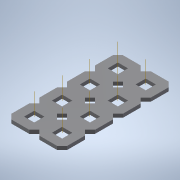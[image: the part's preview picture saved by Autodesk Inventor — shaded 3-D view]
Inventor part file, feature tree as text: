
AUTODESK INVENTOR PART (.ipt)
format: ipt  version: 2020 (Build 240168000, 168)  size: 1,142,784 bytes
history: native  units: in
note: dims shown in document units (in); Inventor stores cm internally (conversion verified against a paired STEP export)
features: other x17, extrude x2, plane x2, split x2, pattern_linear x1, imported_body x1
ambient origin geometry x8: Origin, YZ Plane, XZ Plane, XY Plane, X Axis, Y Axis, Z Axis, Center Point
bodies: Body1 (feature_tree)
feature tree (25):
  other  "Diamond-Pattern"
  other  "Plate"
  extrude  "length cut"  TaperAngle=0.0deg  [1 undecoded]
  extrude  "width cut"  TaperAngle=0.0deg  [1 undecoded]
  other  "constraint axis"
  pattern_linear  "constraint axes"  Spacing1=0.5in  [1 undecoded]
  other  "front plane"
  other  "right plane"
  plane  "Work Plane5"
  split  "Split1"
  plane  "Work Plane6"
  split  "Split2"
  imported_body  "Base1"
  other  "length profile"
  other  "width profile"
  other  "Work Point1"
  other  "Work Axis36"
  other  "Work Axis40"
  other  "Work Axis42"
  other  "back plane"
  other  "left plane"
  other  "Work Axis170"
  other  "Work Axis171"
  other  "Work Axis175"
  other  "Work Axis176"
note: 3 required parameter values undecoded (feature->parameter linkage not recoverable at this tier; creation-order binding heuristic only, values carry confidence <= 0.55)
